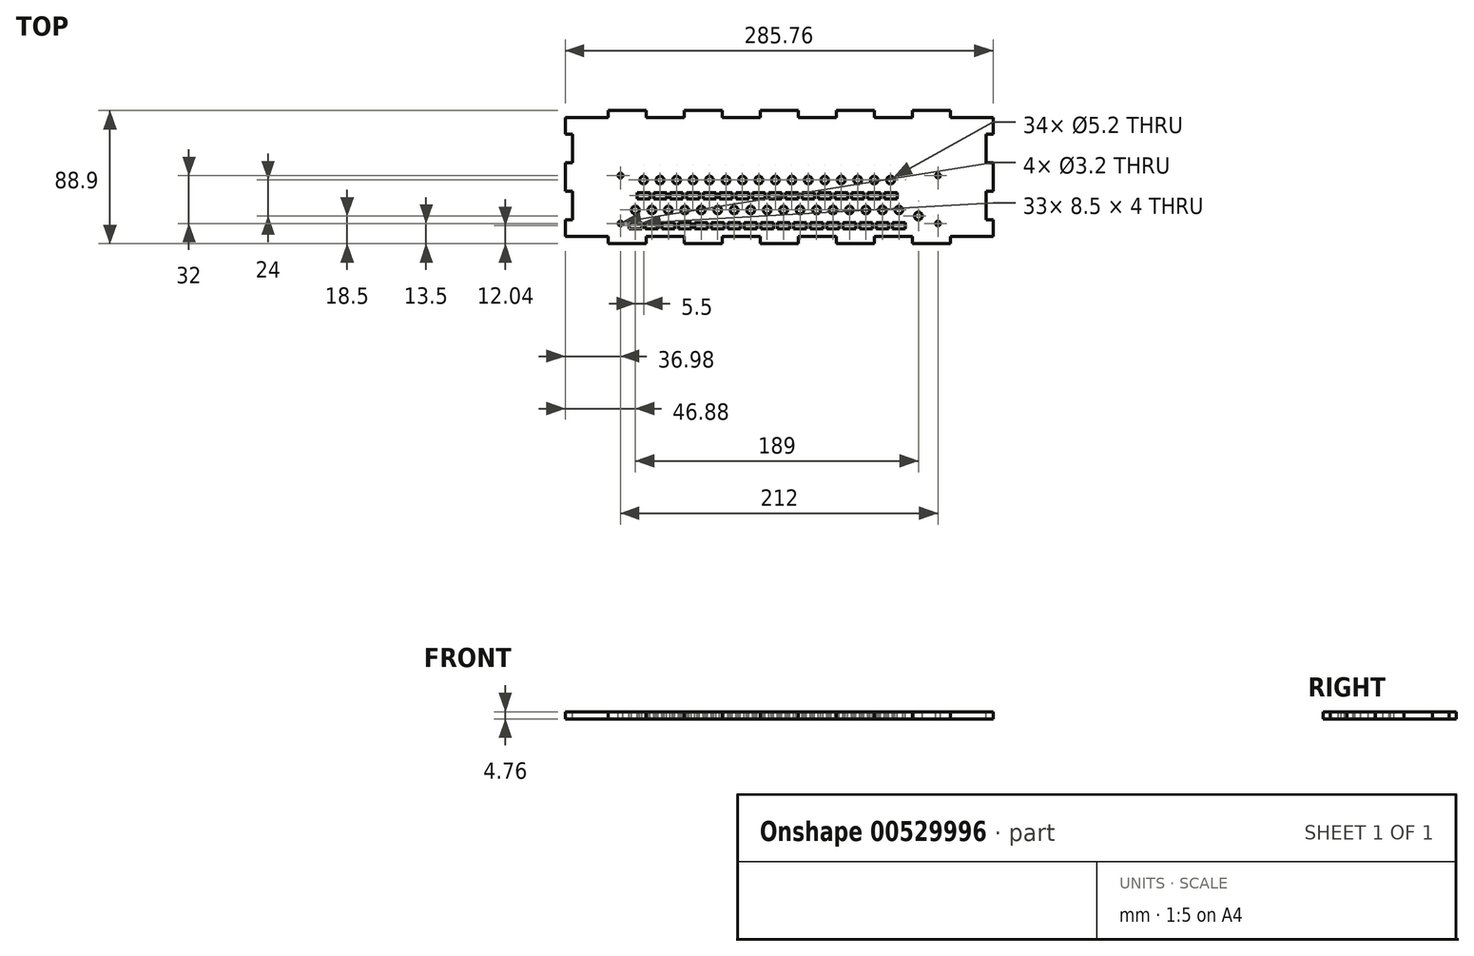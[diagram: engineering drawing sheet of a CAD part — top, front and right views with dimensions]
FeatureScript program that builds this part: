
annotation { "Feature Type Name" : "Feature", "Feature Type Description" : "" }
export const myFeature = defineFeature(function(context is Context, id is Id, definition is map)
    precondition{}
    {
        {
            var Q0;
            Q0=qCreatedBy(makeId("Top.planeOp"),FACE);
            var sketch = newSketch(context, id + "F0", { "sketchPlane" : qUnion([Q0])});
            skLineSegment(sketch, "E0.bottom", {"start": v(-142.87, 44.45) * mm, "end": v(142.88, 44.45) * mm});
            skLineSegment(sketch, "E0.top", {"start": v(-142.87, -44.45) * mm, "end": v(142.87, -44.45) * mm});
            skLineSegment(sketch, "E0.left", {"start": v(-142.88, 44.45) * mm, "end": v(-142.88, -44.45) * mm});
            skLineSegment(sketch, "E0.right", {"start": v(142.88, 44.45) * mm, "end": v(142.88, -44.45) * mm});
            skPoint(sketch, "E0.middle", {"position": v(0, 0) * mm});
            skSolve(sketch);
        }
        {
            var Q0;
            Q0 = qSketchRegion(id + "F0", true);
            extrude(context, id + "F1", {"entities" : qUnion([Q0]), "depth" : 4.76 * mm, "offsetDistance" : 25.4 * mm});
        }
        {
            var Q0;
            Q0=makeQuery(id+"F1.opExtrude","CAP_FACE",FACE,{"disambiguationData":[OSD([sQuery(id+"F0.wireOp",EDGE,"E0.bottom"),sQuery(id+"F0.wireOp",EDGE,"E0.top"),sQuery(id+"F0.wireOp",EDGE,"E0.left"),sQuery(id+"F0.wireOp",EDGE,"E0.right")])],"isStart":false});
            var sketch = newSketch(context, id + "F2", { "sketchPlane" : qUnion([Q0])});
            skLineSegment(sketch, "E1", {"start": v(-110, 44.45) * mm, "end": v(-110, -44.45) * mm, "construction": true});
            skCircle(sketch, "E2", {"center": v(-96, -21.95) * mm, "radius": 2.6 * mm});
            skCircle(sketch, "E3.1.0.0", {"center": v(-85, -21.95) * mm, "radius": 2.6 * mm});
            skCircle(sketch, "E3.2.0.0", {"center": v(-74, -21.95) * mm, "radius": 2.6 * mm});
            skCircle(sketch, "E3.3.0.0", {"center": v(-63, -21.95) * mm, "radius": 2.6 * mm});
            skCircle(sketch, "E3.4.0.0", {"center": v(-52, -21.95) * mm, "radius": 2.6 * mm});
            skCircle(sketch, "E3.5.0.0", {"center": v(-41, -21.95) * mm, "radius": 2.6 * mm});
            skCircle(sketch, "E3.6.0.0", {"center": v(-30, -21.95) * mm, "radius": 2.6 * mm});
            skCircle(sketch, "E3.7.0.0", {"center": v(-19, -21.95) * mm, "radius": 2.6 * mm});
            skCircle(sketch, "E3.8.0.0", {"center": v(-8, -21.95) * mm, "radius": 2.6 * mm});
            skCircle(sketch, "E3.9.0.0", {"center": v(3, -21.95) * mm, "radius": 2.6 * mm});
            skCircle(sketch, "E3.10.0.0", {"center": v(14, -21.95) * mm, "radius": 2.6 * mm});
            skCircle(sketch, "E3.11.0.0", {"center": v(25, -21.95) * mm, "radius": 2.6 * mm});
            skCircle(sketch, "E3.12.0.0", {"center": v(36, -21.95) * mm, "radius": 2.6 * mm});
            skCircle(sketch, "E3.13.0.0", {"center": v(47, -21.95) * mm, "radius": 2.6 * mm});
            skCircle(sketch, "E3.14.0.0", {"center": v(58, -21.95) * mm, "radius": 2.6 * mm});
            skCircle(sketch, "E3.15.0.0", {"center": v(69, -21.95) * mm, "radius": 2.6 * mm});
            skCircle(sketch, "E3.16.0.0", {"center": v(80, -21.95) * mm, "radius": 2.6 * mm});
            skLineSegment(sketch, "E3.direction1", {"start": v(-96, -21.95) * mm, "end": v(-85, -21.95) * mm, "construction": true});
            skCircle(sketch, "E4", {"center": v(-90.5, -1.95) * mm, "radius": 2.6 * mm});
            skCircle(sketch, "E5.1.0.0", {"center": v(-79.5, -1.95) * mm, "radius": 2.6 * mm});
            skCircle(sketch, "E5.2.0.0", {"center": v(-68.5, -1.95) * mm, "radius": 2.6 * mm});
            skCircle(sketch, "E5.3.0.0", {"center": v(-57.5, -1.95) * mm, "radius": 2.6 * mm});
            skCircle(sketch, "E5.4.0.0", {"center": v(-46.5, -1.95) * mm, "radius": 2.6 * mm});
            skCircle(sketch, "E5.5.0.0", {"center": v(-35.5, -1.95) * mm, "radius": 2.6 * mm});
            skCircle(sketch, "E5.6.0.0", {"center": v(-24.5, -1.95) * mm, "radius": 2.6 * mm});
            skCircle(sketch, "E5.7.0.0", {"center": v(-13.5, -1.95) * mm, "radius": 2.6 * mm});
            skCircle(sketch, "E5.8.0.0", {"center": v(-2.5, -1.95) * mm, "radius": 2.6 * mm});
            skCircle(sketch, "E5.9.0.0", {"center": v(8.5, -1.95) * mm, "radius": 2.6 * mm});
            skCircle(sketch, "E5.10.0.0", {"center": v(19.5, -1.95) * mm, "radius": 2.6 * mm});
            skCircle(sketch, "E5.11.0.0", {"center": v(30.5, -1.95) * mm, "radius": 2.6 * mm});
            skCircle(sketch, "E5.12.0.0", {"center": v(41.5, -1.95) * mm, "radius": 2.6 * mm});
            skCircle(sketch, "E5.13.0.0", {"center": v(52.5, -1.95) * mm, "radius": 2.6 * mm});
            skCircle(sketch, "E5.14.0.0", {"center": v(63.5, -1.95) * mm, "radius": 2.6 * mm});
            skCircle(sketch, "E5.15.0.0", {"center": v(74.5, -1.95) * mm, "radius": 2.6 * mm});
            skLineSegment(sketch, "E5.direction1", {"start": v(-90.5, -1.95) * mm, "end": v(-79.5, -1.95) * mm, "construction": true});
            skCircle(sketch, "E6", {"center": v(93, -25.95) * mm, "radius": 2.6 * mm});
            skSolve(sketch);
        }
        {
            var Q0;
            Q0 = qSketchRegion(id + "F2", true);
            extrude(context, id + "F3", {"entities" : qUnion([Q0]), "operationType" : NewBodyOperationType.REMOVE, "oppositeDirection" : true, "depth" : 25.4 * mm, "offsetDistance" : 25.4 * mm});
        }
        {
            var Q0;
            Q0=makeQuery(id+"F1.opExtrude","CAP_FACE",FACE,{"disambiguationData":[OSD([sQuery(id+"F0.wireOp",EDGE,"E0.bottom"),sQuery(id+"F0.wireOp",EDGE,"E0.top"),sQuery(id+"F0.wireOp",EDGE,"E0.left"),sQuery(id+"F0.wireOp",EDGE,"E0.right")])],"isStart":false});
            var sketch = newSketch(context, id + "F4", { "sketchPlane" : qUnion([Q0])});
            skLineSegment(sketch, "E7", {"start": v(-96, -21.95) * mm, "end": v(-96, -30.45) * mm, "construction": true});
            skLineSegment(sketch, "E8.bottom", {"start": v(-100.25, -30.41) * mm, "end": v(-91.75, -30.41) * mm});
            skLineSegment(sketch, "E8.top", {"start": v(-100.25, -34.41) * mm, "end": v(-91.75, -34.41) * mm});
            skLineSegment(sketch, "E8.left", {"start": v(-100.25, -30.41) * mm, "end": v(-100.25, -34.41) * mm});
            skLineSegment(sketch, "E8.right", {"start": v(-91.75, -30.41) * mm, "end": v(-91.75, -34.41) * mm});
            skLineSegment(sketch, "E9", {"start": v(-96, -30.41) * mm, "end": v(-96, -34.41) * mm, "construction": true});
            skLineSegment(sketch, "E10", {"start": v(-96, -34.41) * mm, "end": v(-96, -32.41) * mm, "construction": true});
            skLineSegment(sketch, "E11", {"start": v(-96, -32.41) * mm, "end": v(-100.25, -32.41) * mm, "construction": true});
            skLineSegment(sketch, "E12.1.0.0", {"start": v(-85, -34.41) * mm, "end": v(-85, -32.41) * mm, "construction": true});
            skLineSegment(sketch, "E12.1.0.1", {"start": v(-89.25, -30.41) * mm, "end": v(-80.75, -30.41) * mm});
            skLineSegment(sketch, "E12.1.0.2", {"start": v(-89.25, -30.41) * mm, "end": v(-89.25, -34.41) * mm});
            skLineSegment(sketch, "E12.1.0.3", {"start": v(-89.25, -34.41) * mm, "end": v(-80.75, -34.41) * mm});
            skLineSegment(sketch, "E12.1.0.4", {"start": v(-80.75, -30.41) * mm, "end": v(-80.75, -34.41) * mm});
            skLineSegment(sketch, "E12.2.0.0", {"start": v(-74, -34.41) * mm, "end": v(-74, -32.41) * mm, "construction": true});
            skLineSegment(sketch, "E12.2.0.1", {"start": v(-78.25, -30.41) * mm, "end": v(-69.75, -30.41) * mm});
            skLineSegment(sketch, "E12.2.0.2", {"start": v(-78.25, -30.41) * mm, "end": v(-78.25, -34.41) * mm});
            skLineSegment(sketch, "E12.2.0.3", {"start": v(-78.25, -34.41) * mm, "end": v(-69.75, -34.41) * mm});
            skLineSegment(sketch, "E12.2.0.4", {"start": v(-69.75, -30.41) * mm, "end": v(-69.75, -34.41) * mm});
            skLineSegment(sketch, "E12.3.0.0", {"start": v(-63, -34.41) * mm, "end": v(-63, -32.41) * mm, "construction": true});
            skLineSegment(sketch, "E12.3.0.1", {"start": v(-67.25, -30.41) * mm, "end": v(-58.75, -30.41) * mm});
            skLineSegment(sketch, "E12.3.0.2", {"start": v(-67.25, -30.41) * mm, "end": v(-67.25, -34.41) * mm});
            skLineSegment(sketch, "E12.3.0.3", {"start": v(-67.25, -34.41) * mm, "end": v(-58.75, -34.41) * mm});
            skLineSegment(sketch, "E12.3.0.4", {"start": v(-58.75, -30.41) * mm, "end": v(-58.75, -34.41) * mm});
            skLineSegment(sketch, "E12.4.0.0", {"start": v(-52, -34.41) * mm, "end": v(-52, -32.41) * mm, "construction": true});
            skLineSegment(sketch, "E12.4.0.1", {"start": v(-56.25, -30.41) * mm, "end": v(-47.75, -30.41) * mm});
            skLineSegment(sketch, "E12.4.0.2", {"start": v(-56.25, -30.41) * mm, "end": v(-56.25, -34.41) * mm});
            skLineSegment(sketch, "E12.4.0.3", {"start": v(-56.25, -34.41) * mm, "end": v(-47.75, -34.41) * mm});
            skLineSegment(sketch, "E12.4.0.4", {"start": v(-47.75, -30.41) * mm, "end": v(-47.75, -34.41) * mm});
            skLineSegment(sketch, "E12.5.0.0", {"start": v(-41, -34.41) * mm, "end": v(-41, -32.41) * mm, "construction": true});
            skLineSegment(sketch, "E12.5.0.1", {"start": v(-45.25, -30.41) * mm, "end": v(-36.75, -30.41) * mm});
            skLineSegment(sketch, "E12.5.0.2", {"start": v(-45.25, -30.41) * mm, "end": v(-45.25, -34.41) * mm});
            skLineSegment(sketch, "E12.5.0.3", {"start": v(-45.25, -34.41) * mm, "end": v(-36.75, -34.41) * mm});
            skLineSegment(sketch, "E12.5.0.4", {"start": v(-36.75, -30.41) * mm, "end": v(-36.75, -34.41) * mm});
            skLineSegment(sketch, "E12.6.0.0", {"start": v(-30, -34.41) * mm, "end": v(-30, -32.41) * mm, "construction": true});
            skLineSegment(sketch, "E12.6.0.1", {"start": v(-34.25, -30.41) * mm, "end": v(-25.75, -30.41) * mm});
            skLineSegment(sketch, "E12.6.0.2", {"start": v(-34.25, -30.41) * mm, "end": v(-34.25, -34.41) * mm});
            skLineSegment(sketch, "E12.6.0.3", {"start": v(-34.25, -34.41) * mm, "end": v(-25.75, -34.41) * mm});
            skLineSegment(sketch, "E12.6.0.4", {"start": v(-25.75, -30.41) * mm, "end": v(-25.75, -34.41) * mm});
            skLineSegment(sketch, "E12.7.0.0", {"start": v(-19, -34.41) * mm, "end": v(-19, -32.41) * mm, "construction": true});
            skLineSegment(sketch, "E12.7.0.1", {"start": v(-23.25, -30.41) * mm, "end": v(-14.75, -30.41) * mm});
            skLineSegment(sketch, "E12.7.0.2", {"start": v(-23.25, -30.41) * mm, "end": v(-23.25, -34.41) * mm});
            skLineSegment(sketch, "E12.7.0.3", {"start": v(-23.25, -34.41) * mm, "end": v(-14.75, -34.41) * mm});
            skLineSegment(sketch, "E12.7.0.4", {"start": v(-14.75, -30.41) * mm, "end": v(-14.75, -34.41) * mm});
            skLineSegment(sketch, "E12.8.0.0", {"start": v(-8, -34.41) * mm, "end": v(-8, -32.41) * mm, "construction": true});
            skLineSegment(sketch, "E12.8.0.1", {"start": v(-12.25, -30.41) * mm, "end": v(-3.75, -30.41) * mm});
            skLineSegment(sketch, "E12.8.0.2", {"start": v(-12.25, -30.41) * mm, "end": v(-12.25, -34.41) * mm});
            skLineSegment(sketch, "E12.8.0.3", {"start": v(-12.25, -34.41) * mm, "end": v(-3.75, -34.41) * mm});
            skLineSegment(sketch, "E12.8.0.4", {"start": v(-3.75, -30.41) * mm, "end": v(-3.75, -34.41) * mm});
            skLineSegment(sketch, "E12.9.0.0", {"start": v(3, -34.41) * mm, "end": v(3, -32.41) * mm, "construction": true});
            skLineSegment(sketch, "E12.9.0.1", {"start": v(-1.25, -30.41) * mm, "end": v(7.25, -30.41) * mm});
            skLineSegment(sketch, "E12.9.0.2", {"start": v(-1.25, -30.41) * mm, "end": v(-1.25, -34.41) * mm});
            skLineSegment(sketch, "E12.9.0.3", {"start": v(-1.25, -34.41) * mm, "end": v(7.25, -34.41) * mm});
            skLineSegment(sketch, "E12.9.0.4", {"start": v(7.25, -30.41) * mm, "end": v(7.25, -34.41) * mm});
            skLineSegment(sketch, "E12.10.0.0", {"start": v(14, -34.41) * mm, "end": v(14, -32.41) * mm, "construction": true});
            skLineSegment(sketch, "E12.10.0.1", {"start": v(9.75, -30.41) * mm, "end": v(18.25, -30.41) * mm});
            skLineSegment(sketch, "E12.10.0.2", {"start": v(9.75, -30.41) * mm, "end": v(9.75, -34.41) * mm});
            skLineSegment(sketch, "E12.10.0.3", {"start": v(9.75, -34.41) * mm, "end": v(18.25, -34.41) * mm});
            skLineSegment(sketch, "E12.10.0.4", {"start": v(18.25, -30.41) * mm, "end": v(18.25, -34.41) * mm});
            skLineSegment(sketch, "E12.11.0.0", {"start": v(25, -34.41) * mm, "end": v(25, -32.41) * mm, "construction": true});
            skLineSegment(sketch, "E12.11.0.1", {"start": v(20.75, -30.41) * mm, "end": v(29.25, -30.41) * mm});
            skLineSegment(sketch, "E12.11.0.2", {"start": v(20.75, -30.41) * mm, "end": v(20.75, -34.41) * mm});
            skLineSegment(sketch, "E12.11.0.3", {"start": v(20.75, -34.41) * mm, "end": v(29.25, -34.41) * mm});
            skLineSegment(sketch, "E12.11.0.4", {"start": v(29.25, -30.41) * mm, "end": v(29.25, -34.41) * mm});
            skLineSegment(sketch, "E12.12.0.0", {"start": v(36, -34.41) * mm, "end": v(36, -32.41) * mm, "construction": true});
            skLineSegment(sketch, "E12.12.0.1", {"start": v(31.75, -30.41) * mm, "end": v(40.25, -30.41) * mm});
            skLineSegment(sketch, "E12.12.0.2", {"start": v(31.75, -30.41) * mm, "end": v(31.75, -34.41) * mm});
            skLineSegment(sketch, "E12.12.0.3", {"start": v(31.75, -34.41) * mm, "end": v(40.25, -34.41) * mm});
            skLineSegment(sketch, "E12.12.0.4", {"start": v(40.25, -30.41) * mm, "end": v(40.25, -34.41) * mm});
            skLineSegment(sketch, "E12.13.0.0", {"start": v(47, -34.41) * mm, "end": v(47, -32.41) * mm, "construction": true});
            skLineSegment(sketch, "E12.13.0.1", {"start": v(42.75, -30.41) * mm, "end": v(51.25, -30.41) * mm});
            skLineSegment(sketch, "E12.13.0.2", {"start": v(42.75, -30.41) * mm, "end": v(42.75, -34.41) * mm});
            skLineSegment(sketch, "E12.13.0.3", {"start": v(42.75, -34.41) * mm, "end": v(51.25, -34.41) * mm});
            skLineSegment(sketch, "E12.13.0.4", {"start": v(51.25, -30.41) * mm, "end": v(51.25, -34.41) * mm});
            skLineSegment(sketch, "E12.14.0.0", {"start": v(58, -34.41) * mm, "end": v(58, -32.41) * mm, "construction": true});
            skLineSegment(sketch, "E12.14.0.1", {"start": v(53.75, -30.41) * mm, "end": v(62.25, -30.41) * mm});
            skLineSegment(sketch, "E12.14.0.2", {"start": v(53.75, -30.41) * mm, "end": v(53.75, -34.41) * mm});
            skLineSegment(sketch, "E12.14.0.3", {"start": v(53.75, -34.41) * mm, "end": v(62.25, -34.41) * mm});
            skLineSegment(sketch, "E12.14.0.4", {"start": v(62.25, -30.41) * mm, "end": v(62.25, -34.41) * mm});
            skLineSegment(sketch, "E12.15.0.0", {"start": v(69, -34.41) * mm, "end": v(69, -32.41) * mm, "construction": true});
            skLineSegment(sketch, "E12.15.0.1", {"start": v(64.75, -30.41) * mm, "end": v(73.25, -30.41) * mm});
            skLineSegment(sketch, "E12.15.0.2", {"start": v(64.75, -30.41) * mm, "end": v(64.75, -34.41) * mm});
            skLineSegment(sketch, "E12.15.0.3", {"start": v(64.75, -34.41) * mm, "end": v(73.25, -34.41) * mm});
            skLineSegment(sketch, "E12.15.0.4", {"start": v(73.25, -30.41) * mm, "end": v(73.25, -34.41) * mm});
            skLineSegment(sketch, "E12.16.0.0", {"start": v(80, -34.41) * mm, "end": v(80, -32.41) * mm, "construction": true});
            skLineSegment(sketch, "E12.16.0.1", {"start": v(75.75, -30.41) * mm, "end": v(84.25, -30.41) * mm});
            skLineSegment(sketch, "E12.16.0.2", {"start": v(75.75, -30.41) * mm, "end": v(75.75, -34.41) * mm});
            skLineSegment(sketch, "E12.16.0.3", {"start": v(75.75, -34.41) * mm, "end": v(84.25, -34.41) * mm});
            skLineSegment(sketch, "E12.16.0.4", {"start": v(84.25, -30.41) * mm, "end": v(84.25, -34.41) * mm});
            skLineSegment(sketch, "E12.direction1", {"start": v(-96, -34.41) * mm, "end": v(-85, -34.41) * mm, "construction": true});
            skLineSegment(sketch, "E13", {"start": v(-90.5, -1.95) * mm, "end": v(-90.5, -10.32) * mm, "construction": true});
            skLineSegment(sketch, "E14.bottom", {"start": v(-94.75, -10.41) * mm, "end": v(-86.25, -10.41) * mm});
            skLineSegment(sketch, "E14.top", {"start": v(-94.75, -14.41) * mm, "end": v(-86.25, -14.41) * mm});
            skLineSegment(sketch, "E14.left", {"start": v(-94.75, -10.41) * mm, "end": v(-94.75, -14.41) * mm});
            skLineSegment(sketch, "E14.right", {"start": v(-86.25, -10.41) * mm, "end": v(-86.25, -14.41) * mm});
            skLineSegment(sketch, "E15", {"start": v(-90.5, -10.41) * mm, "end": v(-90.5, -14.41) * mm, "construction": true});
            skLineSegment(sketch, "E16", {"start": v(-90.5, -14.41) * mm, "end": v(-90.5, -12.41) * mm, "construction": true});
            skLineSegment(sketch, "E17", {"start": v(-90.5, -12.41) * mm, "end": v(-94.75, -12.41) * mm, "construction": true});
            skLineSegment(sketch, "E18.1.0.0", {"start": v(-79.5, -10.41) * mm, "end": v(-79.5, -14.41) * mm, "construction": true});
            skLineSegment(sketch, "E18.1.0.1", {"start": v(-83.75, -10.41) * mm, "end": v(-75.25, -10.41) * mm});
            skLineSegment(sketch, "E18.1.0.2", {"start": v(-83.75, -10.41) * mm, "end": v(-83.75, -14.41) * mm});
            skLineSegment(sketch, "E18.1.0.3", {"start": v(-83.75, -14.41) * mm, "end": v(-75.25, -14.41) * mm});
            skLineSegment(sketch, "E18.1.0.4", {"start": v(-75.25, -10.41) * mm, "end": v(-75.25, -14.41) * mm});
            skLineSegment(sketch, "E18.2.0.0", {"start": v(-68.5, -10.41) * mm, "end": v(-68.5, -14.41) * mm, "construction": true});
            skLineSegment(sketch, "E18.2.0.1", {"start": v(-72.75, -10.41) * mm, "end": v(-64.25, -10.41) * mm});
            skLineSegment(sketch, "E18.2.0.2", {"start": v(-72.75, -10.41) * mm, "end": v(-72.75, -14.41) * mm});
            skLineSegment(sketch, "E18.2.0.3", {"start": v(-72.75, -14.41) * mm, "end": v(-64.25, -14.41) * mm});
            skLineSegment(sketch, "E18.2.0.4", {"start": v(-64.25, -10.41) * mm, "end": v(-64.25, -14.41) * mm});
            skLineSegment(sketch, "E18.3.0.0", {"start": v(-57.5, -10.41) * mm, "end": v(-57.5, -14.41) * mm, "construction": true});
            skLineSegment(sketch, "E18.3.0.1", {"start": v(-61.75, -10.41) * mm, "end": v(-53.25, -10.41) * mm});
            skLineSegment(sketch, "E18.3.0.2", {"start": v(-61.75, -10.41) * mm, "end": v(-61.75, -14.41) * mm});
            skLineSegment(sketch, "E18.3.0.3", {"start": v(-61.75, -14.41) * mm, "end": v(-53.25, -14.41) * mm});
            skLineSegment(sketch, "E18.3.0.4", {"start": v(-53.25, -10.41) * mm, "end": v(-53.25, -14.41) * mm});
            skLineSegment(sketch, "E18.4.0.0", {"start": v(-46.5, -10.41) * mm, "end": v(-46.5, -14.41) * mm, "construction": true});
            skLineSegment(sketch, "E18.4.0.1", {"start": v(-50.75, -10.41) * mm, "end": v(-42.25, -10.41) * mm});
            skLineSegment(sketch, "E18.4.0.2", {"start": v(-50.75, -10.41) * mm, "end": v(-50.75, -14.41) * mm});
            skLineSegment(sketch, "E18.4.0.3", {"start": v(-50.75, -14.41) * mm, "end": v(-42.25, -14.41) * mm});
            skLineSegment(sketch, "E18.4.0.4", {"start": v(-42.25, -10.41) * mm, "end": v(-42.25, -14.41) * mm});
            skLineSegment(sketch, "E18.5.0.0", {"start": v(-35.5, -10.41) * mm, "end": v(-35.5, -14.41) * mm, "construction": true});
            skLineSegment(sketch, "E18.5.0.1", {"start": v(-39.75, -10.41) * mm, "end": v(-31.25, -10.41) * mm});
            skLineSegment(sketch, "E18.5.0.2", {"start": v(-39.75, -10.41) * mm, "end": v(-39.75, -14.41) * mm});
            skLineSegment(sketch, "E18.5.0.3", {"start": v(-39.75, -14.41) * mm, "end": v(-31.25, -14.41) * mm});
            skLineSegment(sketch, "E18.5.0.4", {"start": v(-31.25, -10.41) * mm, "end": v(-31.25, -14.41) * mm});
            skLineSegment(sketch, "E18.6.0.0", {"start": v(-24.5, -10.41) * mm, "end": v(-24.5, -14.41) * mm, "construction": true});
            skLineSegment(sketch, "E18.6.0.1", {"start": v(-28.75, -10.41) * mm, "end": v(-20.25, -10.41) * mm});
            skLineSegment(sketch, "E18.6.0.2", {"start": v(-28.75, -10.41) * mm, "end": v(-28.75, -14.41) * mm});
            skLineSegment(sketch, "E18.6.0.3", {"start": v(-28.75, -14.41) * mm, "end": v(-20.25, -14.41) * mm});
            skLineSegment(sketch, "E18.6.0.4", {"start": v(-20.25, -10.41) * mm, "end": v(-20.25, -14.41) * mm});
            skLineSegment(sketch, "E18.7.0.0", {"start": v(-13.5, -10.41) * mm, "end": v(-13.5, -14.41) * mm, "construction": true});
            skLineSegment(sketch, "E18.7.0.1", {"start": v(-17.75, -10.41) * mm, "end": v(-9.25, -10.41) * mm});
            skLineSegment(sketch, "E18.7.0.2", {"start": v(-17.75, -10.41) * mm, "end": v(-17.75, -14.41) * mm});
            skLineSegment(sketch, "E18.7.0.3", {"start": v(-17.75, -14.41) * mm, "end": v(-9.25, -14.41) * mm});
            skLineSegment(sketch, "E18.7.0.4", {"start": v(-9.25, -10.41) * mm, "end": v(-9.25, -14.41) * mm});
            skLineSegment(sketch, "E18.8.0.0", {"start": v(-2.5, -10.41) * mm, "end": v(-2.5, -14.41) * mm, "construction": true});
            skLineSegment(sketch, "E18.8.0.1", {"start": v(-6.75, -10.41) * mm, "end": v(1.75, -10.41) * mm});
            skLineSegment(sketch, "E18.8.0.2", {"start": v(-6.75, -10.41) * mm, "end": v(-6.75, -14.41) * mm});
            skLineSegment(sketch, "E18.8.0.3", {"start": v(-6.75, -14.41) * mm, "end": v(1.75, -14.41) * mm});
            skLineSegment(sketch, "E18.8.0.4", {"start": v(1.75, -10.41) * mm, "end": v(1.75, -14.41) * mm});
            skLineSegment(sketch, "E18.9.0.0", {"start": v(8.5, -10.41) * mm, "end": v(8.5, -14.41) * mm, "construction": true});
            skLineSegment(sketch, "E18.9.0.1", {"start": v(4.25, -10.41) * mm, "end": v(12.75, -10.41) * mm});
            skLineSegment(sketch, "E18.9.0.2", {"start": v(4.25, -10.41) * mm, "end": v(4.25, -14.41) * mm});
            skLineSegment(sketch, "E18.9.0.3", {"start": v(4.25, -14.41) * mm, "end": v(12.75, -14.41) * mm});
            skLineSegment(sketch, "E18.9.0.4", {"start": v(12.75, -10.41) * mm, "end": v(12.75, -14.41) * mm});
            skLineSegment(sketch, "E18.10.0.0", {"start": v(19.5, -10.41) * mm, "end": v(19.5, -14.41) * mm, "construction": true});
            skLineSegment(sketch, "E18.10.0.1", {"start": v(15.25, -10.41) * mm, "end": v(23.75, -10.41) * mm});
            skLineSegment(sketch, "E18.10.0.2", {"start": v(15.25, -10.41) * mm, "end": v(15.25, -14.41) * mm});
            skLineSegment(sketch, "E18.10.0.3", {"start": v(15.25, -14.41) * mm, "end": v(23.75, -14.41) * mm});
            skLineSegment(sketch, "E18.10.0.4", {"start": v(23.75, -10.41) * mm, "end": v(23.75, -14.41) * mm});
            skLineSegment(sketch, "E18.11.0.0", {"start": v(30.5, -10.41) * mm, "end": v(30.5, -14.41) * mm, "construction": true});
            skLineSegment(sketch, "E18.11.0.1", {"start": v(26.25, -10.41) * mm, "end": v(34.75, -10.41) * mm});
            skLineSegment(sketch, "E18.11.0.2", {"start": v(26.25, -10.41) * mm, "end": v(26.25, -14.41) * mm});
            skLineSegment(sketch, "E18.11.0.3", {"start": v(26.25, -14.41) * mm, "end": v(34.75, -14.41) * mm});
            skLineSegment(sketch, "E18.11.0.4", {"start": v(34.75, -10.41) * mm, "end": v(34.75, -14.41) * mm});
            skLineSegment(sketch, "E18.12.0.0", {"start": v(41.5, -10.41) * mm, "end": v(41.5, -14.41) * mm, "construction": true});
            skLineSegment(sketch, "E18.12.0.1", {"start": v(37.25, -10.41) * mm, "end": v(45.75, -10.41) * mm});
            skLineSegment(sketch, "E18.12.0.2", {"start": v(37.25, -10.41) * mm, "end": v(37.25, -14.41) * mm});
            skLineSegment(sketch, "E18.12.0.3", {"start": v(37.25, -14.41) * mm, "end": v(45.75, -14.41) * mm});
            skLineSegment(sketch, "E18.12.0.4", {"start": v(45.75, -10.41) * mm, "end": v(45.75, -14.41) * mm});
            skLineSegment(sketch, "E18.13.0.0", {"start": v(52.5, -10.41) * mm, "end": v(52.5, -14.41) * mm, "construction": true});
            skLineSegment(sketch, "E18.13.0.1", {"start": v(48.25, -10.41) * mm, "end": v(56.75, -10.41) * mm});
            skLineSegment(sketch, "E18.13.0.2", {"start": v(48.25, -10.41) * mm, "end": v(48.25, -14.41) * mm});
            skLineSegment(sketch, "E18.13.0.3", {"start": v(48.25, -14.41) * mm, "end": v(56.75, -14.41) * mm});
            skLineSegment(sketch, "E18.13.0.4", {"start": v(56.75, -10.41) * mm, "end": v(56.75, -14.41) * mm});
            skLineSegment(sketch, "E18.14.0.0", {"start": v(63.5, -10.41) * mm, "end": v(63.5, -14.41) * mm, "construction": true});
            skLineSegment(sketch, "E18.14.0.1", {"start": v(59.25, -10.41) * mm, "end": v(67.75, -10.41) * mm});
            skLineSegment(sketch, "E18.14.0.2", {"start": v(59.25, -10.41) * mm, "end": v(59.25, -14.41) * mm});
            skLineSegment(sketch, "E18.14.0.3", {"start": v(59.25, -14.41) * mm, "end": v(67.75, -14.41) * mm});
            skLineSegment(sketch, "E18.14.0.4", {"start": v(67.75, -10.41) * mm, "end": v(67.75, -14.41) * mm});
            skLineSegment(sketch, "E18.15.0.0", {"start": v(74.5, -10.41) * mm, "end": v(74.5, -14.41) * mm, "construction": true});
            skLineSegment(sketch, "E18.15.0.1", {"start": v(70.25, -10.41) * mm, "end": v(78.75, -10.41) * mm});
            skLineSegment(sketch, "E18.15.0.2", {"start": v(70.25, -10.41) * mm, "end": v(70.25, -14.41) * mm});
            skLineSegment(sketch, "E18.15.0.3", {"start": v(70.25, -14.41) * mm, "end": v(78.75, -14.41) * mm});
            skLineSegment(sketch, "E18.15.0.4", {"start": v(78.75, -10.41) * mm, "end": v(78.75, -14.41) * mm});
            skLineSegment(sketch, "E18.direction1", {"start": v(-90.5, -14.41) * mm, "end": v(-79.5, -14.41) * mm, "construction": true});
            skSolve(sketch);
        }
        {
            var Q0;
            Q0 = qSketchRegion(id + "F4", true);
            extrude(context, id + "F5", {"entities" : qUnion([Q0]), "operationType" : NewBodyOperationType.REMOVE, "oppositeDirection" : true, "depth" : 25.4 * mm, "offsetDistance" : 25.4 * mm});
        }
        {
            var Q0;
            Q0=makeQuery(id+"F1.opExtrude","CAP_FACE",FACE,{"disambiguationData":[OSD([sQuery(id+"F0.wireOp",EDGE,"E0.bottom"),sQuery(id+"F0.wireOp",EDGE,"E0.top"),sQuery(id+"F0.wireOp",EDGE,"E0.left"),sQuery(id+"F0.wireOp",EDGE,"E0.right")])],"isStart":false});
            var sketch = newSketch(context, id + "F6", { "sketchPlane" : qUnion([Q0])});
            skLineSegment(sketch, "E19", {"start": v(-109.9, 44.45) * mm, "end": v(-109.9, -44.45) * mm, "construction": true});
            skCircle(sketch, "E20", {"center": v(-105.9, -30.95) * mm, "radius": 1.6 * mm});
            skCircle(sketch, "E21.0", {"center": v(-96, -21.95) * mm, "radius": 2.6 * mm, "construction": true});
            skCircle(sketch, "E22.0.1.0", {"center": v(-105.9, 1.05) * mm, "radius": 1.6 * mm});
            skCircle(sketch, "E22.1.0.0", {"center": v(106.1, -30.95) * mm, "radius": 1.6 * mm});
            skCircle(sketch, "E22.1.1.0", {"center": v(106.1, 1.05) * mm, "radius": 1.6 * mm});
            skLineSegment(sketch, "E22.direction1", {"start": v(-105.9, -30.95) * mm, "end": v(106.1, -30.95) * mm, "construction": true});
            skLineSegment(sketch, "E22.direction2", {"start": v(-105.9, -30.95) * mm, "end": v(-105.9, 1.05) * mm, "construction": true});
            skSolve(sketch);
        }
        {
            var Q0;
            Q0 = qSketchRegion(id + "F6", true);
            extrude(context, id + "F7", {"entities" : qUnion([Q0]), "operationType" : NewBodyOperationType.REMOVE, "oppositeDirection" : true, "depth" : 25.4 * mm, "offsetDistance" : 25.4 * mm});
        }
        {
            var Q0;
            Q0=makeQuery(id+"F1.opExtrude","CAP_FACE",FACE,{"disambiguationData":[OSD([sQuery(id+"F0.wireOp",EDGE,"E0.bottom"),sQuery(id+"F0.wireOp",EDGE,"E0.top"),sQuery(id+"F0.wireOp",EDGE,"E0.left"),sQuery(id+"F0.wireOp",EDGE,"E0.right")])],"isStart":false});
            var sketch = newSketch(context, id + "F8", { "sketchPlane" : qUnion([Q0])});
            skLineSegment(sketch, "E23", {"start": v(0, 0) * mm, "end": v(0, 44.45) * mm, "construction": true});
            skLineSegment(sketch, "E24", {"start": v(-25.4, 44.45) * mm, "end": v(-25.4, 72.92) * mm, "construction": true});
            skLineSegment(sketch, "E25.bottom", {"start": v(-38.1, 44.45) * mm, "end": v(-12.7, 44.45) * mm});
            skLineSegment(sketch, "E25.top", {"start": v(-38.1, 39.69) * mm, "end": v(-12.7, 39.69) * mm});
            skLineSegment(sketch, "E25.left", {"start": v(-38.1, 44.45) * mm, "end": v(-38.1, 39.69) * mm});
            skLineSegment(sketch, "E25.right", {"start": v(-12.7, 44.45) * mm, "end": v(-12.7, 39.69) * mm});
            skLineSegment(sketch, "E26", {"start": v(-25.4, 44.45) * mm, "end": v(-25.4, 39.69) * mm, "construction": true});
            skLineSegment(sketch, "E27.1.0.0", {"start": v(-76.2, 44.45) * mm, "end": v(-76.2, 39.69) * mm, "construction": true});
            skLineSegment(sketch, "E27.1.0.1", {"start": v(-88.9, 44.45) * mm, "end": v(-88.9, 39.69) * mm});
            skLineSegment(sketch, "E27.1.0.2", {"start": v(-88.9, 44.45) * mm, "end": v(-63.5, 44.45) * mm});
            skLineSegment(sketch, "E27.1.0.3", {"start": v(-88.9, 39.69) * mm, "end": v(-63.5, 39.69) * mm});
            skLineSegment(sketch, "E27.1.0.4", {"start": v(-63.5, 44.45) * mm, "end": v(-63.5, 39.69) * mm});
            skLineSegment(sketch, "E27.2.0.0", {"start": v(-127, 44.45) * mm, "end": v(-127, 39.69) * mm, "construction": true});
            skLineSegment(sketch, "E27.2.0.2", {"start": v(-139.7, 44.45) * mm, "end": v(-114.3, 44.45) * mm});
            skLineSegment(sketch, "E27.2.0.3", {"start": v(-139.7, 39.69) * mm, "end": v(-114.3, 39.69) * mm});
            skLineSegment(sketch, "E27.2.0.4", {"start": v(-114.3, 44.45) * mm, "end": v(-114.3, 39.69) * mm});
            skLineSegment(sketch, "E27.direction1", {"start": v(-25.4, 39.69) * mm, "end": v(-76.2, 39.69) * mm, "construction": true});
            skLineSegment(sketch, "E28", {"start": v(-139.7, 44.45) * mm, "end": v(-142.87, 44.45) * mm});
            skLineSegment(sketch, "E29", {"start": v(-139.7, 39.69) * mm, "end": v(-142.88, 39.69) * mm});
            skLineSegment(sketch, "E30", {"start": v(-142.88, 39.69) * mm, "end": v(-142.88, 44.45) * mm});
            skLineSegment(sketch, "E31.MirrorCS", {"start": v(139.7, 44.45) * mm, "end": v(142.88, 44.45) * mm});
            skLineSegment(sketch, "E32.MirrorCS", {"start": v(38.1, 44.45) * mm, "end": v(38.1, 39.69) * mm});
            skLineSegment(sketch, "E33.MirrorCS", {"start": v(12.7, 44.45) * mm, "end": v(12.7, 39.69) * mm});
            skLineSegment(sketch, "E34.MirrorCS", {"start": v(25.4, 44.45) * mm, "end": v(25.4, 39.69) * mm, "construction": true});
            skLineSegment(sketch, "E35.MirrorCS", {"start": v(88.9, 44.45) * mm, "end": v(88.9, 39.69) * mm});
            skLineSegment(sketch, "E36.MirrorCS", {"start": v(139.7, 39.69) * mm, "end": v(142.88, 39.69) * mm});
            skLineSegment(sketch, "E37.MirrorCS", {"start": v(63.5, 44.45) * mm, "end": v(63.5, 39.69) * mm});
            skLineSegment(sketch, "E38.MirrorCS", {"start": v(142.88, 39.69) * mm, "end": v(142.88, 44.45) * mm});
            skLineSegment(sketch, "E39.MirrorCS", {"start": v(114.3, 44.45) * mm, "end": v(114.3, 39.69) * mm});
            skLineSegment(sketch, "E40.MirrorCS", {"start": v(76.2, 44.45) * mm, "end": v(76.2, 39.69) * mm, "construction": true});
            skLineSegment(sketch, "E41.MirrorCS", {"start": v(127, 44.45) * mm, "end": v(127, 39.69) * mm, "construction": true});
            skLineSegment(sketch, "E42.MirrorCS", {"start": v(25.4, 39.69) * mm, "end": v(76.2, 39.69) * mm, "construction": true});
            skLineSegment(sketch, "E43.MirrorCS", {"start": v(38.1, 39.69) * mm, "end": v(12.7, 39.69) * mm});
            skLineSegment(sketch, "E44.MirrorCS", {"start": v(88.9, 44.45) * mm, "end": v(63.5, 44.45) * mm});
            skLineSegment(sketch, "E45.MirrorCS", {"start": v(139.7, 39.69) * mm, "end": v(114.3, 39.69) * mm});
            skLineSegment(sketch, "E46.MirrorCS", {"start": v(38.1, 44.45) * mm, "end": v(12.7, 44.45) * mm});
            skLineSegment(sketch, "E47.MirrorCS", {"start": v(88.9, 39.69) * mm, "end": v(63.5, 39.69) * mm});
            skLineSegment(sketch, "E48.MirrorCS", {"start": v(139.7, 44.45) * mm, "end": v(114.3, 44.45) * mm});
            skLineSegment(sketch, "E49", {"start": v(0, 0) * mm, "end": v(142.88, 0) * mm, "construction": true});
            skLineSegment(sketch, "E50.MirrorCS", {"start": v(88.9, -44.45) * mm, "end": v(88.9, -39.69) * mm});
            skLineSegment(sketch, "E51.MirrorCS", {"start": v(-139.7, -39.69) * mm, "end": v(-142.88, -39.69) * mm});
            skLineSegment(sketch, "E52.MirrorCS", {"start": v(-114.3, -44.45) * mm, "end": v(-114.3, -39.69) * mm});
            skLineSegment(sketch, "E53.MirrorCS", {"start": v(139.7, -39.69) * mm, "end": v(142.88, -39.69) * mm});
            skLineSegment(sketch, "E54.MirrorCS", {"start": v(-38.1, -44.45) * mm, "end": v(-38.1, -39.69) * mm});
            skLineSegment(sketch, "E55.MirrorCS", {"start": v(-12.7, -44.45) * mm, "end": v(-12.7, -39.69) * mm});
            skLineSegment(sketch, "E56.MirrorCS", {"start": v(-25.4, -44.45) * mm, "end": v(-25.4, -39.69) * mm, "construction": true});
            skLineSegment(sketch, "E57.MirrorCS", {"start": v(-88.9, -44.45) * mm, "end": v(-88.9, -39.69) * mm});
            skLineSegment(sketch, "E58.MirrorCS", {"start": v(-139.7, -44.45) * mm, "end": v(-142.87, -44.45) * mm});
            skLineSegment(sketch, "E59.MirrorCS", {"start": v(12.7, -44.45) * mm, "end": v(12.7, -39.69) * mm});
            skLineSegment(sketch, "E60.MirrorCS", {"start": v(38.1, -44.45) * mm, "end": v(38.1, -39.69) * mm});
            skLineSegment(sketch, "E61.MirrorCS", {"start": v(142.88, -39.69) * mm, "end": v(142.88, -44.45) * mm});
            skLineSegment(sketch, "E62.MirrorCS", {"start": v(139.7, -44.45) * mm, "end": v(142.88, -44.45) * mm});
            skLineSegment(sketch, "E63.MirrorCS", {"start": v(63.5, -44.45) * mm, "end": v(63.5, -39.69) * mm});
            skLineSegment(sketch, "E64.MirrorCS", {"start": v(114.3, -44.45) * mm, "end": v(114.3, -39.69) * mm});
            skLineSegment(sketch, "E65.MirrorCS", {"start": v(-142.88, -39.69) * mm, "end": v(-142.88, -44.45) * mm});
            skLineSegment(sketch, "E66.MirrorCS", {"start": v(-63.5, -44.45) * mm, "end": v(-63.5, -39.69) * mm});
            skLineSegment(sketch, "E67.MirrorCS", {"start": v(-76.2, -44.45) * mm, "end": v(-76.2, -39.69) * mm, "construction": true});
            skLineSegment(sketch, "E68.MirrorCS", {"start": v(25.4, -44.45) * mm, "end": v(25.4, -39.69) * mm, "construction": true});
            skLineSegment(sketch, "E69.MirrorCS", {"start": v(38.1, -39.69) * mm, "end": v(12.7, -39.69) * mm});
            skLineSegment(sketch, "E70.MirrorCS", {"start": v(-127, -44.45) * mm, "end": v(-127, -39.69) * mm, "construction": true});
            skLineSegment(sketch, "E71.MirrorCS", {"start": v(76.2, -44.45) * mm, "end": v(76.2, -39.69) * mm, "construction": true});
            skLineSegment(sketch, "E72.MirrorCS", {"start": v(127, -44.45) * mm, "end": v(127, -39.69) * mm, "construction": true});
            skLineSegment(sketch, "E73.MirrorCS", {"start": v(139.7, -39.69) * mm, "end": v(114.3, -39.69) * mm});
            skLineSegment(sketch, "E74.MirrorCS", {"start": v(-139.7, -44.45) * mm, "end": v(-114.3, -44.45) * mm});
            skLineSegment(sketch, "E75.MirrorCS", {"start": v(-139.7, -39.69) * mm, "end": v(-114.3, -39.69) * mm});
            skLineSegment(sketch, "E76.MirrorCS", {"start": v(-38.1, -44.45) * mm, "end": v(-12.7, -44.45) * mm});
            skLineSegment(sketch, "E77.MirrorCS", {"start": v(-38.1, -39.69) * mm, "end": v(-12.7, -39.69) * mm});
            skLineSegment(sketch, "E78.MirrorCS", {"start": v(-88.9, -44.45) * mm, "end": v(-63.5, -44.45) * mm});
            skLineSegment(sketch, "E79.MirrorCS", {"start": v(-88.9, -39.69) * mm, "end": v(-63.5, -39.69) * mm});
            skLineSegment(sketch, "E80.MirrorCS", {"start": v(88.9, -44.45) * mm, "end": v(63.5, -44.45) * mm});
            skLineSegment(sketch, "E81.MirrorCS", {"start": v(-25.4, -39.69) * mm, "end": v(-76.2, -39.69) * mm, "construction": true});
            skLineSegment(sketch, "E82.MirrorCS", {"start": v(25.4, -39.69) * mm, "end": v(76.2, -39.69) * mm, "construction": true});
            skLineSegment(sketch, "E83.MirrorCS", {"start": v(88.9, -39.69) * mm, "end": v(63.5, -39.69) * mm});
            skLineSegment(sketch, "E84.MirrorCS", {"start": v(38.1, -44.45) * mm, "end": v(12.7, -44.45) * mm});
            skLineSegment(sketch, "E85.MirrorCS", {"start": v(139.7, -44.45) * mm, "end": v(114.3, -44.45) * mm});
            skSolve(sketch);
        }
        {
            var Q0;
            Q0 = qSketchRegion(id + "F8", true);
            extrude(context, id + "F9", {"entities" : qUnion([Q0]), "operationType" : NewBodyOperationType.REMOVE, "oppositeDirection" : true, "depth" : 25.4 * mm, "offsetDistance" : 25.4 * mm});
        }
        {
            var Q0;
            Q0=makeQuery(id+"F1.opExtrude","CAP_FACE",FACE,{"disambiguationData":[OSD([sQuery(id+"F0.wireOp",EDGE,"E0.bottom"),sQuery(id+"F0.wireOp",EDGE,"E0.top"),sQuery(id+"F0.wireOp",EDGE,"E0.left"),sQuery(id+"F0.wireOp",EDGE,"E0.right")])],"isStart":false});
            var sketch = newSketch(context, id + "F10", { "sketchPlane" : qUnion([Q0])});
            skLineSegment(sketch, "E86", {"start": v(0, 0) * mm, "end": v(-142.88, 0) * mm, "construction": true});
            skLineSegment(sketch, "E87.direction1", {"start": v(-142.88, 0) * mm, "end": v(-117.47, 0) * mm, "construction": true});
            skLineSegment(sketch, "E88", {"start": v(0, 3.87) * mm, "end": v(0, 44.45) * mm, "construction": true});
            skLineSegment(sketch, "E89", {"start": v(-142.88, 19.05) * mm, "end": v(-181.93, 19.05) * mm, "construction": true});
            skLineSegment(sketch, "E90.bottom", {"start": v(-142.88, 28.58) * mm, "end": v(-138.11, 28.58) * mm});
            skLineSegment(sketch, "E90.top", {"start": v(-142.88, 9.53) * mm, "end": v(-138.11, 9.53) * mm});
            skLineSegment(sketch, "E90.left", {"start": v(-142.88, 28.57) * mm, "end": v(-142.88, 9.53) * mm});
            skLineSegment(sketch, "E90.right", {"start": v(-138.11, 28.57) * mm, "end": v(-138.11, 9.52) * mm});
            skLineSegment(sketch, "E91", {"start": v(-142.88, 19.05) * mm, "end": v(-138.11, 19.05) * mm, "construction": true});
            skLineSegment(sketch, "E92.MirrorCS", {"start": v(-142.88, -19.05) * mm, "end": v(-181.93, -19.05) * mm, "construction": true});
            skLineSegment(sketch, "E93.MirrorCS", {"start": v(-142.88, -28.58) * mm, "end": v(-138.11, -28.58) * mm});
            skLineSegment(sketch, "E94.MirrorCS", {"start": v(-142.88, -19.05) * mm, "end": v(-138.11, -19.05) * mm, "construction": true});
            skLineSegment(sketch, "E95.MirrorCS", {"start": v(-138.11, -28.58) * mm, "end": v(-138.11, -9.53) * mm});
            skLineSegment(sketch, "E96.MirrorCS", {"start": v(-142.88, -28.58) * mm, "end": v(-142.88, -9.53) * mm});
            skLineSegment(sketch, "E97.MirrorCS", {"start": v(-142.88, -9.53) * mm, "end": v(-138.11, -9.53) * mm});
            skLineSegment(sketch, "E98.MirrorCS", {"start": v(0, -3.87) * mm, "end": v(0, -44.45) * mm, "construction": true});
            skLineSegment(sketch, "E99.MirrorCS", {"start": v(142.88, 28.57) * mm, "end": v(142.88, 9.52) * mm});
            skLineSegment(sketch, "E100.MirrorCS", {"start": v(138.11, 28.57) * mm, "end": v(138.11, 9.52) * mm});
            skLineSegment(sketch, "E101.MirrorCS", {"start": v(138.11, -28.58) * mm, "end": v(138.11, -9.53) * mm});
            skLineSegment(sketch, "E102.MirrorCS", {"start": v(142.88, -19.05) * mm, "end": v(138.11, -19.05) * mm, "construction": true});
            skLineSegment(sketch, "E103.MirrorCS", {"start": v(142.88, -28.58) * mm, "end": v(138.11, -28.58) * mm});
            skLineSegment(sketch, "E104.MirrorCS", {"start": v(142.88, 19.05) * mm, "end": v(138.11, 19.05) * mm, "construction": true});
            skLineSegment(sketch, "E105.MirrorCS", {"start": v(142.88, -28.58) * mm, "end": v(142.88, -9.53) * mm});
            skLineSegment(sketch, "E106.MirrorCS", {"start": v(142.88, 28.57) * mm, "end": v(138.11, 28.57) * mm});
            skLineSegment(sketch, "E107.MirrorCS", {"start": v(142.88, 9.52) * mm, "end": v(138.11, 9.52) * mm});
            skLineSegment(sketch, "E108.MirrorCS", {"start": v(142.88, -9.53) * mm, "end": v(138.11, -9.53) * mm});
            skSolve(sketch);
        }
        {
            var Q0;
            Q0 = qSketchRegion(id + "F10", true);
            extrude(context, id + "F11", {"entities" : qUnion([Q0]), "operationType" : NewBodyOperationType.REMOVE, "oppositeDirection" : true, "depth" : 25.4 * mm, "offsetDistance" : 25.4 * mm});
        }
        {
            var Q0;
            Q0 = qSketchRegion(id + "F10", true);
            extrude(context, id + "F12", {"entities" : qUnion([Q0]), "operationType" : NewBodyOperationType.REMOVE, "oppositeDirection" : true, "depth" : 25.4 * mm, "offsetDistance" : 25.4 * mm});
        }
    });
